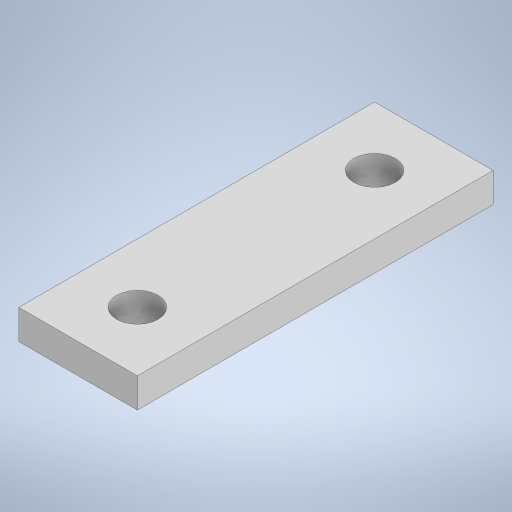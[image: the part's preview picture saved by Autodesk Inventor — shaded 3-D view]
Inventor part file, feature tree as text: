
AUTODESK INVENTOR PART (.ipt)
format: ipt  version: 2023 (Build 270158000, 158)  size: 210,944 bytes
history: native  units: mm
features: other x1, extrude x1, sketch x1
ambient origin geometry x8: Origin, YZ Plane, XZ Plane, XY Plane, X Axis, Y Axis, Z Axis, Center Point
bodies: Body1 (feature_tree)
feature tree (3):
  other  "Sólido1"
  extrude  "Extrusión1"  [1 undecoded]
  sketch  "Boceto1"  dims[d0=2.5mm d1=0.0mm]
note: 1 required parameter value undecoded (feature->parameter linkage not recoverable at this tier; creation-order binding heuristic only, values carry confidence <= 0.55)
